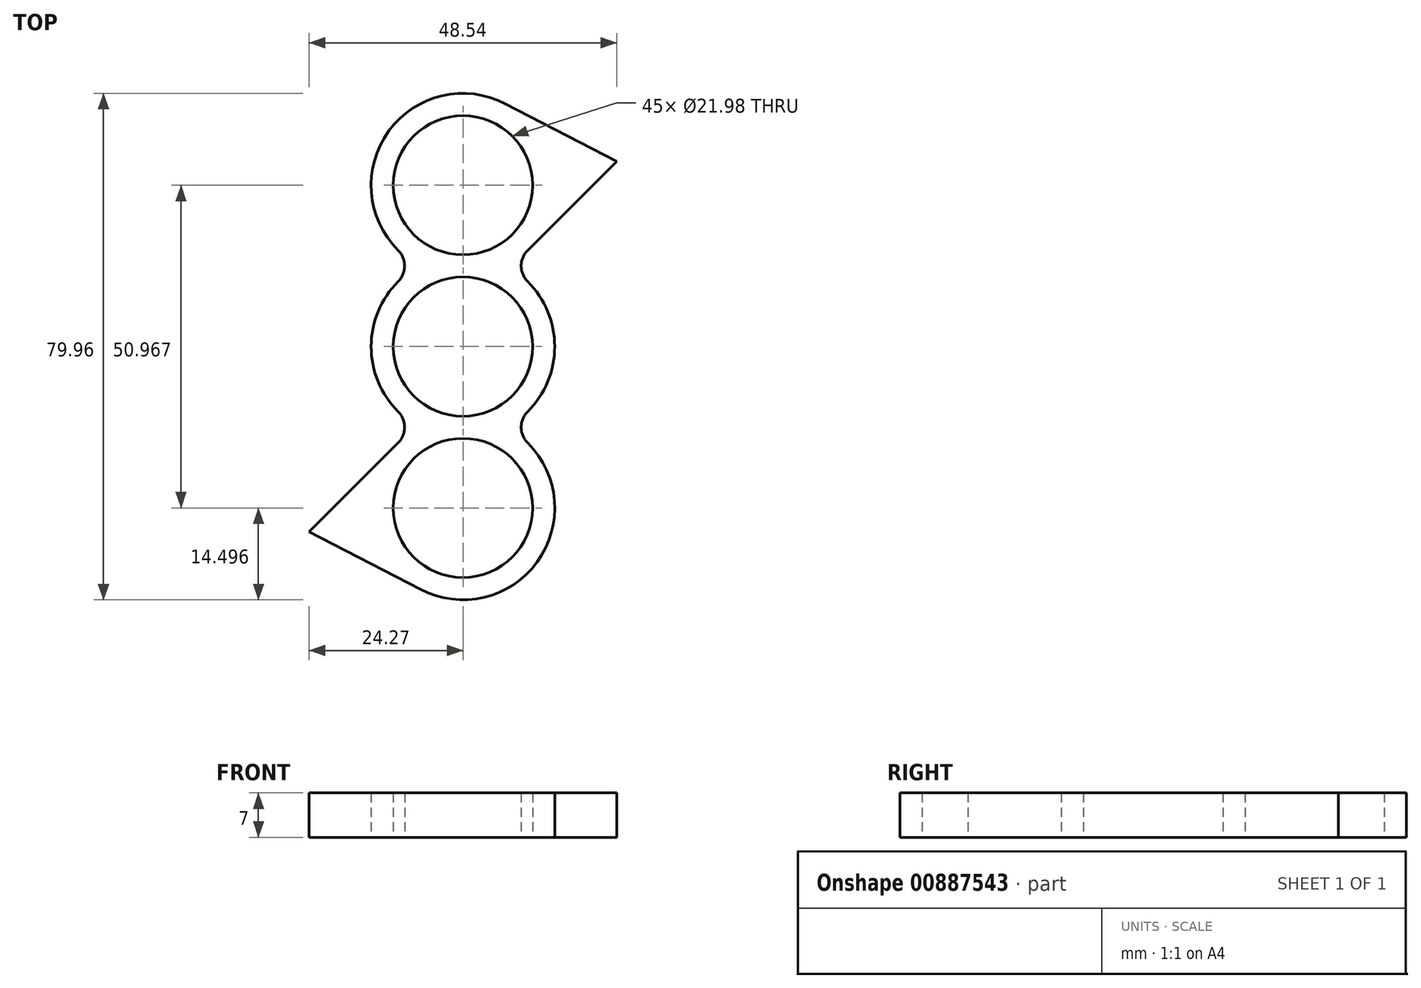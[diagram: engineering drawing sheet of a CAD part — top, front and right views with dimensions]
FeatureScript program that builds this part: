
annotation { "Feature Type Name" : "Feature", "Feature Type Description" : "" }
export const myFeature = defineFeature(function(context is Context, id is Id, definition is map)
    precondition{}
    {
        {
            var Q0;
            Q0=qCreatedBy(makeId("Top.planeOp"),FACE);
            var sketch = newSketch(context, id + "F0", { "sketchPlane" : qUnion([Q0])});
            skCircle(sketch, "E0", {"center": v(0, 0) * mm, "radius": 11 * mm});
            skCircle(sketch, "E1", {"center": v(0, 25.48) * mm, "radius": 11 * mm});
            skCircle(sketch, "E2", {"center": v(0, -25.48) * mm, "radius": 11 * mm});
            skLineSegment(sketch, "E3", {"start": v(0, 25.48) * mm, "end": v(0, -25.48) * mm, "construction": true});
            skLineSegment(sketch, "E4.bottom", {"start": v(-29.85, 57.15) * mm, "end": v(29.85, 57.15) * mm, "construction": true});
            skLineSegment(sketch, "E4.top", {"start": v(-29.85, -57.15) * mm, "end": v(29.85, -57.15) * mm, "construction": true});
            skLineSegment(sketch, "E4.left", {"start": v(-29.84, 57.15) * mm, "end": v(-29.85, -57.15) * mm, "construction": true});
            skLineSegment(sketch, "E4.right", {"start": v(29.85, 57.15) * mm, "end": v(29.84, -57.15) * mm, "construction": true});
            skPoint(sketch, "E5", {"position": v(0, 57.15) * mm});
            skPoint(sketch, "E6", {"position": v(-29.85, 0) * mm});
            skSolve(sketch);
        }
        {
            var Q0;
            Q0=qCreatedBy(makeId("Top.planeOp"),FACE);
            var sketch = newSketch(context, id + "F1", { "sketchPlane" : qUnion([Q0])});
            skCircle(sketch, "E7", {"center": v(0, 25.48) * mm, "radius": 11 * mm});
            skCircle(sketch, "E8", {"center": v(0, 0) * mm, "radius": 11 * mm});
            skCircle(sketch, "E9", {"center": v(0, -25.48) * mm, "radius": 11 * mm});
            skLineSegment(sketch, "E10.bottom", {"start": v(-29.85, 57.15) * mm, "end": v(29.84, 57.15) * mm, "construction": true});
            skLineSegment(sketch, "E10.top", {"start": v(-29.85, -57.15) * mm, "end": v(29.84, -57.15) * mm, "construction": true});
            skLineSegment(sketch, "E10.left", {"start": v(-29.85, 57.15) * mm, "end": v(-29.85, -57.15) * mm, "construction": true});
            skLineSegment(sketch, "E10.right", {"start": v(29.85, 57.15) * mm, "end": v(29.85, -57.15) * mm, "construction": true});
            skPoint(sketch, "E11", {"position": v(-29.85, 0) * mm});
            skPoint(sketch, "E12", {"position": v(0, 57.15) * mm});
            skArc(sketch, "E13.0", {"start": v(10.23, 35.75) * mm, "mid": v(-10.26, 35.72) * mm, "end": v(-10.23, 15.22) * mm});
            skArc(sketch, "E14.0", {"start": v(-10.23, 10.26) * mm, "mid": v(-14.5, 0) * mm, "end": v(-10.23, -10.26) * mm});
            skArc(sketch, "E15.0", {"start": v(-6.68, -38.35) * mm, "mid": v(11.7, -34.04) * mm, "end": v(10.23, -15.22) * mm});
            skArc(sketch, "E16.trimOffspring", {"start": v(10.23, -10.26) * mm, "mid": v(14.5, 0) * mm, "end": v(10.23, 10.26) * mm});
            skPoint(sketch, "E17.visualSharp", {"position": v(-6.9, 12.74) * mm});
            skArc(sketch, "E17.filletArc", {"start": v(-10.23, 10.26) * mm, "mid": v(-9.2, 12.74) * mm, "end": v(-10.23, 15.22) * mm});
            skPoint(sketch, "E18.visualSharp", {"position": v(6.9, 12.74) * mm});
            skArc(sketch, "E18.filletArc", {"start": v(10.23, 15.22) * mm, "mid": v(9.2, 12.74) * mm, "end": v(10.23, 10.26) * mm});
            skPoint(sketch, "E19.visualSharp", {"position": v(6.9, -12.74) * mm});
            skArc(sketch, "E19.filletArc", {"start": v(10.23, -10.26) * mm, "mid": v(9.2, -12.74) * mm, "end": v(10.23, -15.22) * mm});
            skPoint(sketch, "E20.visualSharp", {"position": v(-6.9, -12.74) * mm});
            skArc(sketch, "E20.filletArc", {"start": v(-10.23, -15.22) * mm, "mid": v(-9.2, -12.74) * mm, "end": v(-10.23, -10.26) * mm});
            skPoint(sketch, "E21.end.orphan", {"position": v(10.23, 35.75) * mm});
            skLineSegment(sketch, "E22", {"start": v(10.23, 15.22) * mm, "end": v(24.27, 29.21) * mm});
            skLineSegment(sketch, "E23", {"start": v(24.27, 29.21) * mm, "end": v(6.68, 38.35) * mm});
            skLineSegment(sketch, "E24", {"start": v(-10.23, -15.22) * mm, "end": v(-24.27, -29.21) * mm});
            skLineSegment(sketch, "E25", {"start": v(-24.27, -29.21) * mm, "end": v(-6.68, -38.35) * mm});
            skSolve(sketch);
        }
        {
            var Q0;
            Q0 = qSketchRegion(id + "F1", true);
            extrude(context, id + "F2", {"entities" : qUnion([Q0]), "depth" : 7 * mm, "offsetDistance" : 25.4 * mm});
        }
    });
